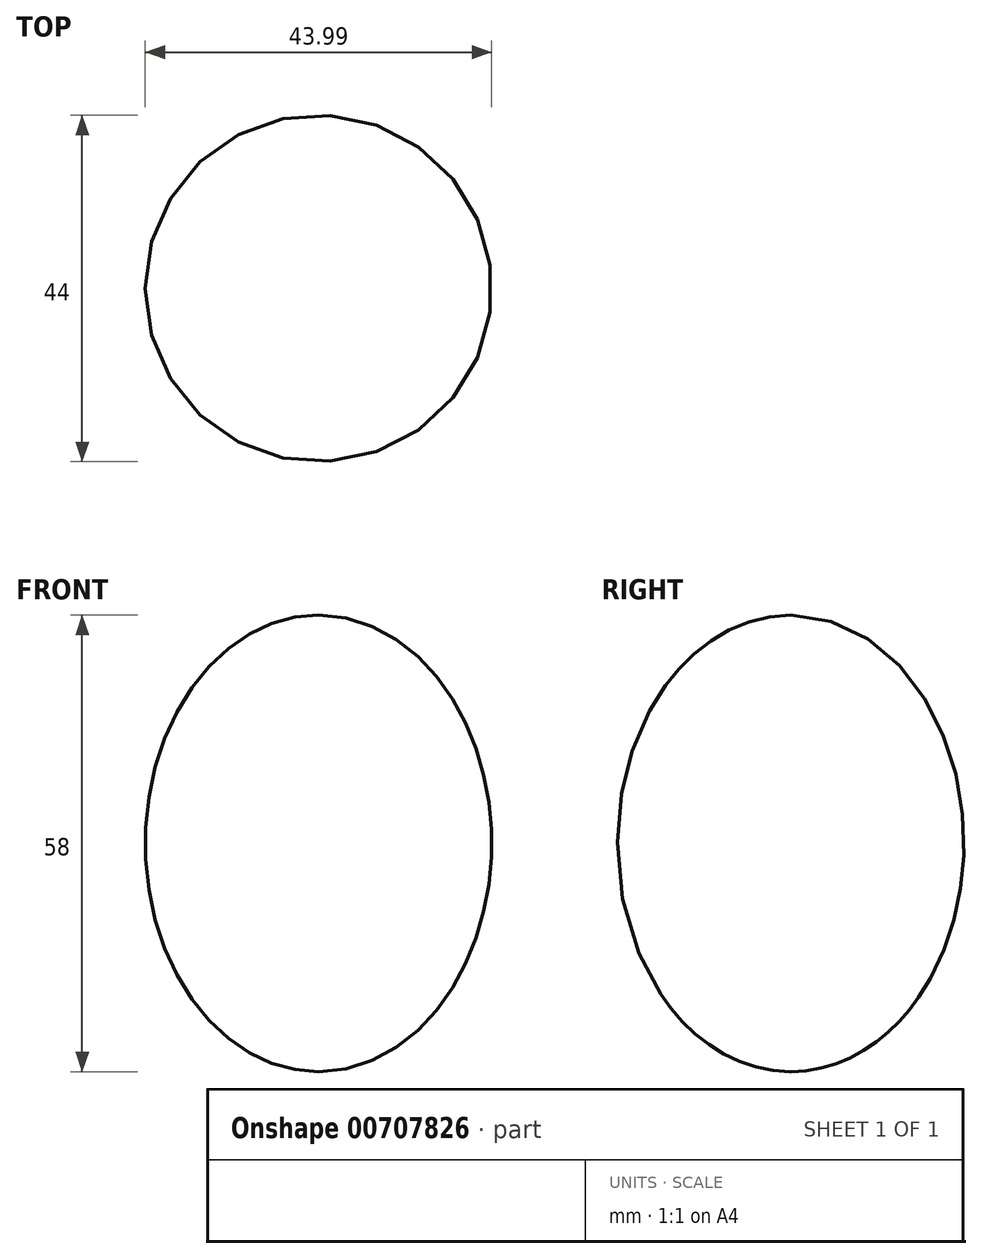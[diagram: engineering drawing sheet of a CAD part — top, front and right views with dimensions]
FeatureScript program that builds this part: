
annotation { "Feature Type Name" : "Feature", "Feature Type Description" : "" }
export const myFeature = defineFeature(function(context is Context, id is Id, definition is map)
    precondition{}
    {
        {
            var Q0;
            Q0=qCreatedBy(makeId("Front.planeOp"),FACE);
            var sketch = newSketch(context, id + "F0", { "sketchPlane" : qUnion([Q0])});
            skEllipticalArc(sketch, "E0", {});
            skLineSegment(sketch, "E1", {"start": v(0, 29) * mm, "end": v(0, -29) * mm});
            const initialGuessF0  = {"E0": [0, 0, 0, 1, 0.029, 0.022, 0, 3.141592653589793]};
            skSetInitialGuess(sketch, initialGuessF0);
            skSolve(sketch);
        }
        {
            var Q0;
            Q0=qCreatedBy(makeId("Front.planeOp"),FACE);
            var sketch = newSketch(context, id + "F1", { "sketchPlane" : qUnion([Q0])});
            skLineSegment(sketch, "E2", {"start": v(0, 41.01) * mm, "end": v(0, -62.13) * mm, "construction": true});
            skSolve(sketch);
        }
        {
            var Q0;
            Q0 = qSketchRegion(id + "F0", true);
            var Q1;
            Q1=sQuery(id+"F1.wireOp",EDGE,"E2");
            revolve(context, id + "F2", {"surfaceOperationType" : NewSurfaceOperationType.NEW, "entities" : qUnion([Q0]), "axis" : qUnion([Q1]), "revolveType" : RevolveType.FULL});
        }
    });
